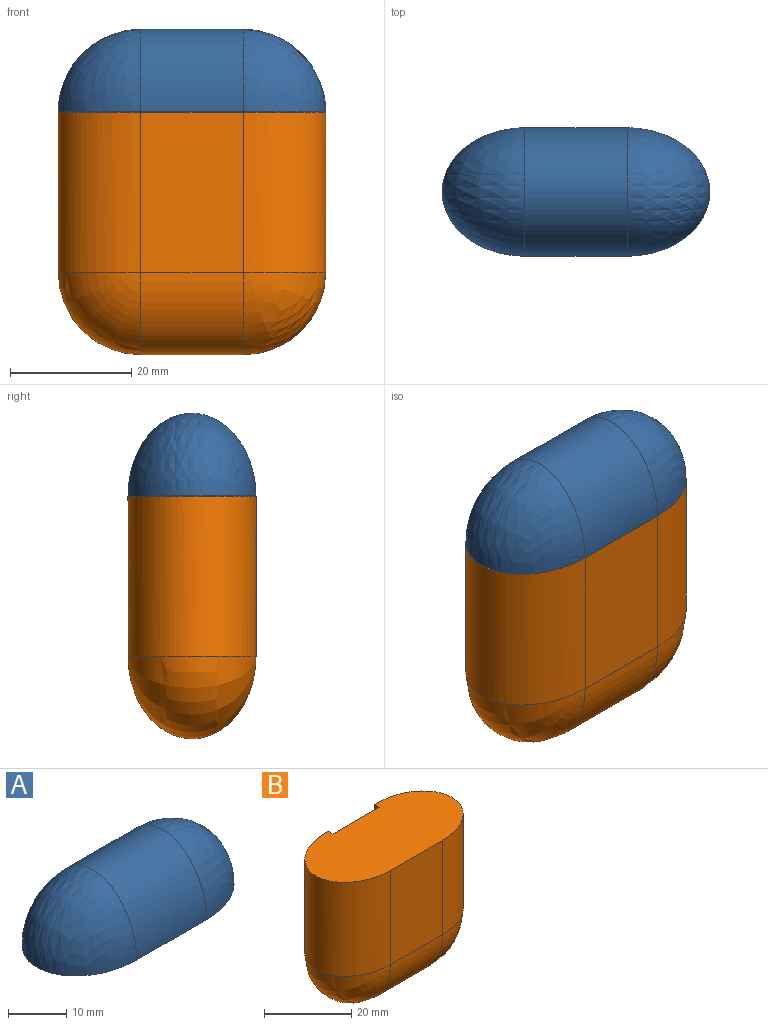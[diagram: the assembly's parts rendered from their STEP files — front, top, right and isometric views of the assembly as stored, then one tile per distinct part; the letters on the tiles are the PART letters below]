
ASSEMBLY  parts=2 mates=1
PART A: 9 faces, bbox 44.1x21.1x16.4 mm
  f0: revolved ~21.1x13.6mm, area 496.4mm2, adj f1,f2
  f1: plane 44.1x21.1mm, normal (0,0,-1), area 785mm2, adj f0,f2,f3,f4,f5,f7
  f2: extruded ~21.1x16.9mm, area 643.7mm2, adj f0,f1,f3,f6
  f3: revolved ~21.1x13.6mm, area 496.4mm2, adj f1,f2
  f4: plane 14.9x2.8mm, normal (0,-1,0), area 41.7mm2, adj f1,f5,f7,f8
  f5: plane 2.8x1.5mm, normal (1,0,0), area 4.2mm2, adj f1,f4,f6,f8
  f6: plane 14.9x2.8mm, normal (0,1,0), area 41.7mm2, adj f2,f5,f7,f8
  f7: plane 2.8x1.5mm, normal (-1,0,0), area 4.2mm2, adj f1,f4,f6,f8
  f8: plane 14.9x1.5mm, normal (0,0,-1), area 22.3mm2, adj f4,f5,f6,f7
PART B: 12 faces, bbox 44.1x21.1x40 mm
  f0: plane 26.4x16.9mm, normal (0,1,0), area 404.4mm2, adj f1,f3,f4,f6,f9,f10,f11
  f1: extruded ~26.4x21.1mm, area 1005.5mm2, adj f0,f2,f4,f5
  f2: plane 26.4x16.9mm, normal (0,-1,0), area 446.2mm2, adj f1,f3,f4,f6
  f3: extruded ~26.4x21.1mm, area 1005.5mm2, adj f0,f2,f4,f7
  f4: plane 44.1x21.1mm, normal (0,0,1), area 785mm2, adj f0,f1,f2,f3,f8,f9,f10
  f5: revolved ~21.1x13.6mm, area 496.4mm2, adj f1,f6
  f6: extruded ~21.1x16.9mm, area 643.7mm2, adj f0,f2,f5,f7
  f7: revolved ~21.1x13.6mm, area 496.4mm2, adj f3,f6
  f8: plane 14.9x2.8mm, normal (0,1,0), area 41.7mm2, adj f4,f9,f10,f11
  f9: plane 2.8x1.5mm, normal (-1,0,0), area 4.2mm2, adj f0,f4,f8,f11
  f10: plane 2.8x1.5mm, normal (1,0,0), area 4.2mm2, adj f0,f4,f8,f11
  f11: plane 14.9x1.5mm, normal (0,0,1), area 22.3mm2, adj f0,f8,f9,f10
PLACE A rot(axis=(-1,0,0),0.3deg) t=(0,0.01,0.05)mm
PLACE B at identity fixed
MATE revolute B.f9 <-> A.f5  axis (-1,0,0) through (7.45,9.52,-1.42)mm
